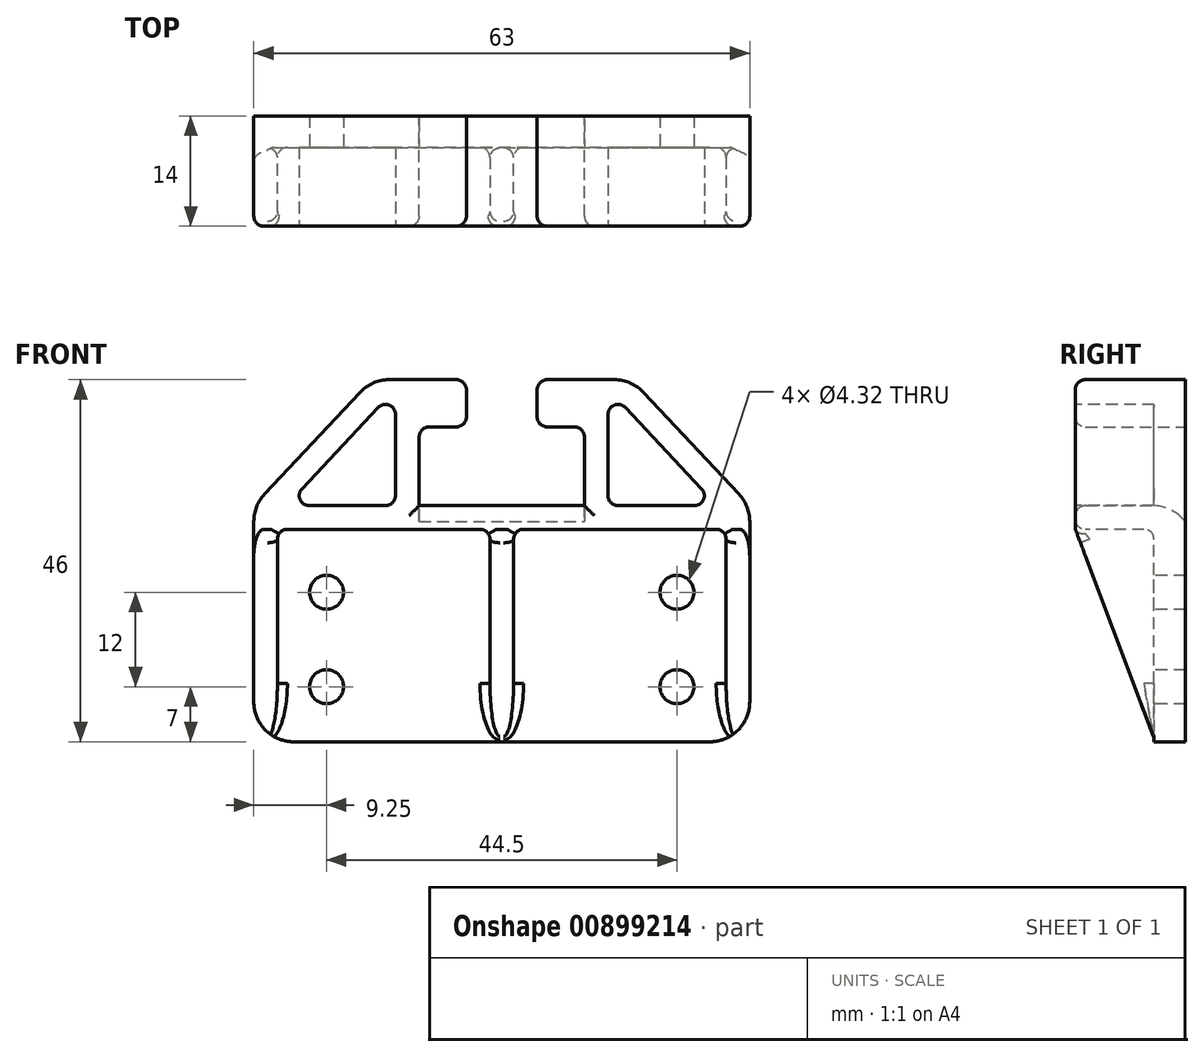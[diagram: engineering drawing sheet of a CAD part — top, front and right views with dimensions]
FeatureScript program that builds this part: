
annotation { "Feature Type Name" : "Feature", "Feature Type Description" : "" }
export const myFeature = defineFeature(function(context is Context, id is Id, definition is map)
    precondition{}
    {
        {
            var Q0;
            Q0=qCreatedBy(makeId("Front.planeOp"),FACE);
            var sketch = newSketch(context, id + "F0", { "sketchPlane" : qUnion([Q0])});
            skLineSegment(sketch, "E0", {"start": v(0, 0) * mm, "end": v(26.42, 0) * mm});
            skLineSegment(sketch, "E1", {"start": v(31.5, 5.08) * mm, "end": v(31.5, 28) * mm});
            skLineSegment(sketch, "E2", {"start": v(30.13, 31.47) * mm, "end": v(18, 44.4) * mm});
            skLineSegment(sketch, "E3", {"start": v(14.3, 46) * mm, "end": v(5.77, 46) * mm});
            skLineSegment(sketch, "E4", {"start": v(4.5, 44.73) * mm, "end": v(4.5, 41.27) * mm});
            skLineSegment(sketch, "E5", {"start": v(5.77, 40) * mm, "end": v(9.23, 40) * mm});
            skLineSegment(sketch, "E6", {"start": v(10.5, 38.73) * mm, "end": v(10.5, 30) * mm});
            skLineSegment(sketch, "E7", {"start": v(10.5, 30) * mm, "end": v(0, 30) * mm});
            skPoint(sketch, "E8.visualSharp", {"position": v(31.5, 0) * mm});
            skArc(sketch, "E8.filletArc", {"start": v(26.42, 0) * mm, "mid": v(30.01, 1.49) * mm, "end": v(31.5, 5.08) * mm});
            skPoint(sketch, "E9.visualSharp", {"position": v(31.5, 30) * mm});
            skArc(sketch, "E9.filletArc", {"start": v(31.5, 28) * mm, "mid": v(31.14, 29.86) * mm, "end": v(30.13, 31.47) * mm});
            skPoint(sketch, "E10.visualSharp", {"position": v(16.5, 46) * mm});
            skArc(sketch, "E10.filletArc", {"start": v(18, 44.4) * mm, "mid": v(16.32, 45.58) * mm, "end": v(14.3, 46) * mm});
            skPoint(sketch, "E11.visualSharp", {"position": v(4.5, 46) * mm});
            skArc(sketch, "E11.filletArc", {"start": v(5.77, 46) * mm, "mid": v(4.87, 45.63) * mm, "end": v(4.5, 44.73) * mm});
            skPoint(sketch, "E12.visualSharp", {"position": v(10.5, 40) * mm});
            skArc(sketch, "E12.filletArc", {"start": v(10.5, 38.73) * mm, "mid": v(10.13, 39.63) * mm, "end": v(9.23, 40) * mm});
            skPoint(sketch, "E13.visualSharp", {"position": v(4.5, 40) * mm});
            skArc(sketch, "E13.filletArc", {"start": v(4.5, 41.27) * mm, "mid": v(4.87, 40.37) * mm, "end": v(5.77, 40) * mm});
            skArc(sketch, "E14.MirrorCS", {"start": v(-5.77, 46) * mm, "mid": v(-4.87, 45.63) * mm, "end": v(-4.5, 44.73) * mm});
            skLineSegment(sketch, "E15.MirrorCS", {"start": v(-30.13, 31.47) * mm, "end": v(-18, 44.4) * mm});
            skArc(sketch, "E16.MirrorCS", {"start": v(-26.42, 0) * mm, "mid": v(-30.01, 1.49) * mm, "end": v(-31.5, 5.08) * mm});
            skLineSegment(sketch, "E17.MirrorCS", {"start": v(-10.5, 38.73) * mm, "end": v(-10.5, 30) * mm});
            skPoint(sketch, "E18.MirrorP", {"position": v(-16.5, 46) * mm});
            skArc(sketch, "E19.MirrorCS", {"start": v(-4.5, 41.27) * mm, "mid": v(-4.87, 40.37) * mm, "end": v(-5.77, 40) * mm});
            skArc(sketch, "E20.MirrorCS", {"start": v(-10.5, 38.73) * mm, "mid": v(-10.13, 39.63) * mm, "end": v(-9.23, 40) * mm});
            skLineSegment(sketch, "E21.MirrorCS", {"start": v(-14.3, 46) * mm, "end": v(-5.77, 46) * mm});
            skArc(sketch, "E22.MirrorCS", {"start": v(-31.5, 28) * mm, "mid": v(-31.14, 29.86) * mm, "end": v(-30.13, 31.47) * mm});
            skPoint(sketch, "E23.MirrorP", {"position": v(-4.5, 46) * mm});
            skLineSegment(sketch, "E24.MirrorCS", {"start": v(0, 0) * mm, "end": v(-26.42, 0) * mm});
            skLineSegment(sketch, "E25.MirrorCS", {"start": v(-4.5, 44.73) * mm, "end": v(-4.5, 41.27) * mm});
            skPoint(sketch, "E26.MirrorP", {"position": v(-10.5, 40) * mm});
            skArc(sketch, "E27.MirrorCS", {"start": v(-18, 44.4) * mm, "mid": v(-16.32, 45.58) * mm, "end": v(-14.3, 46) * mm});
            skLineSegment(sketch, "E28.MirrorCS", {"start": v(-31.5, 5.08) * mm, "end": v(-31.5, 28) * mm});
            skPoint(sketch, "E29.MirrorP", {"position": v(-31.5, 0) * mm});
            skPoint(sketch, "E30.MirrorP", {"position": v(-4.5, 40) * mm});
            skLineSegment(sketch, "E31.MirrorCS", {"start": v(-10.5, 30) * mm, "end": v(0, 30) * mm});
            skLineSegment(sketch, "E32.MirrorCS", {"start": v(-5.77, 40) * mm, "end": v(-9.23, 40) * mm});
            skPoint(sketch, "E33.MirrorP", {"position": v(-31.5, 30) * mm});
            skSolve(sketch);
        }
        {
            var Q0;
            Q0 = qSketchRegion(id + "F0", true);
            extrude(context, id + "F1", {"entities" : qUnion([Q0]), "depth" : 14 * mm, "offsetDistance" : 25.4 * mm});
        }
        {
            var Q0;
            Q0=makeQuery(id+"F1.opExtrude","CAP_FACE",FACE,{"disambiguationData":[OSD([sQuery(id+"F0.wireOp",EDGE,"E0"),sQuery(id+"F0.wireOp",EDGE,"E1"),sQuery(id+"F0.wireOp",EDGE,"E2"),sQuery(id+"F0.wireOp",EDGE,"E3"),sQuery(id+"F0.wireOp",EDGE,"E4"),sQuery(id+"F0.wireOp",EDGE,"E5"),sQuery(id+"F0.wireOp",EDGE,"E6"),sQuery(id+"F0.wireOp",EDGE,"E7"),sQuery(id+"F0.wireOp",EDGE,"E8.filletArc"),sQuery(id+"F0.wireOp",EDGE,"E9.filletArc"),sQuery(id+"F0.wireOp",EDGE,"E10.filletArc"),sQuery(id+"F0.wireOp",EDGE,"E11.filletArc"),sQuery(id+"F0.wireOp",EDGE,"E12.filletArc"),sQuery(id+"F0.wireOp",EDGE,"E13.filletArc"),sQuery(id+"F0.wireOp",EDGE,"E14.MirrorCS"),sQuery(id+"F0.wireOp",EDGE,"E15.MirrorCS"),sQuery(id+"F0.wireOp",EDGE,"E16.MirrorCS"),sQuery(id+"F0.wireOp",EDGE,"E17.MirrorCS"),sQuery(id+"F0.wireOp",EDGE,"E19.MirrorCS"),sQuery(id+"F0.wireOp",EDGE,"E20.MirrorCS"),sQuery(id+"F0.wireOp",EDGE,"E21.MirrorCS"),sQuery(id+"F0.wireOp",EDGE,"E22.MirrorCS"),sQuery(id+"F0.wireOp",EDGE,"E24.MirrorCS"),sQuery(id+"F0.wireOp",EDGE,"E25.MirrorCS"),sQuery(id+"F0.wireOp",EDGE,"E27.MirrorCS"),sQuery(id+"F0.wireOp",EDGE,"E28.MirrorCS"),sQuery(id+"F0.wireOp",EDGE,"E31.MirrorCS"),sQuery(id+"F0.wireOp",EDGE,"E32.MirrorCS")])],"isStart":false});
            var sketch = newSketch(context, id + "F2", { "sketchPlane" : qUnion([Q0])});
            skLineSegment(sketch, "E34.bottom", {"start": v(22.25, 7) * mm, "end": v(-22.25, 7) * mm});
            skLineSegment(sketch, "E34.top", {"start": v(22.25, 19) * mm, "end": v(-22.25, 19) * mm});
            skLineSegment(sketch, "E34.left", {"start": v(22.25, 7) * mm, "end": v(22.25, 19) * mm});
            skLineSegment(sketch, "E34.right", {"start": v(-22.25, 7) * mm, "end": v(-22.25, 19) * mm});
            skPoint(sketch, "E34.middle", {"position": v(0, 13) * mm});
            skLineSegment(sketch, "E35", {"start": v(0, 0) * mm, "end": v(0, 13) * mm});
            skSolve(sketch);
        }
        {
            var Q0;
            Q0=sQuery(id+"F2.wireOp",VERTEX,"E34.right.end");
            var Q1;
            Q1=sQuery(id+"F2.wireOp",VERTEX,"E34.top.start");
            var Q2;
            Q2=sQuery(id+"F2.wireOp",VERTEX,"E34.bottom.start");
            var Q3;
            Q3=sQuery(id+"F2.wireOp",VERTEX,"E34.right.start");
            var Q4;
            Q4=makeQuery(id+"F1.opExtrude","SWEPT_BODY",BODY,{"disambiguationData":[OSD([sQuery(id+"F0.wireOp",EDGE,"E0"),sQuery(id+"F0.wireOp",EDGE,"E1"),sQuery(id+"F0.wireOp",EDGE,"E2"),sQuery(id+"F0.wireOp",EDGE,"E3"),sQuery(id+"F0.wireOp",EDGE,"E4"),sQuery(id+"F0.wireOp",EDGE,"E5"),sQuery(id+"F0.wireOp",EDGE,"E6"),sQuery(id+"F0.wireOp",EDGE,"E7"),sQuery(id+"F0.wireOp",EDGE,"E8.filletArc"),sQuery(id+"F0.wireOp",EDGE,"E9.filletArc"),sQuery(id+"F0.wireOp",EDGE,"E10.filletArc"),sQuery(id+"F0.wireOp",EDGE,"E11.filletArc"),sQuery(id+"F0.wireOp",EDGE,"E12.filletArc"),sQuery(id+"F0.wireOp",EDGE,"E13.filletArc"),sQuery(id+"F0.wireOp",EDGE,"E14.MirrorCS"),sQuery(id+"F0.wireOp",EDGE,"E15.MirrorCS"),sQuery(id+"F0.wireOp",EDGE,"E16.MirrorCS"),sQuery(id+"F0.wireOp",EDGE,"E17.MirrorCS"),sQuery(id+"F0.wireOp",EDGE,"E19.MirrorCS"),sQuery(id+"F0.wireOp",EDGE,"E20.MirrorCS"),sQuery(id+"F0.wireOp",EDGE,"E21.MirrorCS"),sQuery(id+"F0.wireOp",EDGE,"E22.MirrorCS"),sQuery(id+"F0.wireOp",EDGE,"E24.MirrorCS"),sQuery(id+"F0.wireOp",EDGE,"E25.MirrorCS"),sQuery(id+"F0.wireOp",EDGE,"E27.MirrorCS"),sQuery(id+"F0.wireOp",EDGE,"E28.MirrorCS"),sQuery(id+"F0.wireOp",EDGE,"E31.MirrorCS"),sQuery(id+"F0.wireOp",EDGE,"E32.MirrorCS")])]});
            hole(context, id + "F3", {"style" : HoleStyle.SIMPLE, "endStyle" : HoleEndStyle.THROUGH, "standardTappedOrClearance" : lookupTablePath({ "standard" : "ANSI", "fit" : "Normal (ASME)", "size" : "#6", "type" : "Clearance" }), "standardBlindInLast" : lookupTablePath({ "fit" : "Normal", "standard" : "ANSI", "size" : "#6", "type" : "Clearance" }), "holeDiameter" : 4.32 * mm, "majorDiameter" : 6.35 * mm, "isTappedThrough" : true, "tappedDepth" : 12.7 * mm, "tapClearance" : 3, "locations" : qUnion([Q0, Q1, Q2, Q3]), "scope" : qUnion([Q4])});
        }
        {
            var Q0;
            Q0=makeQuery(id+"F1.opExtrude","CAP_FACE",FACE,{"disambiguationData":[OSD([sQuery(id+"F0.wireOp",EDGE,"E0"),sQuery(id+"F0.wireOp",EDGE,"E1"),sQuery(id+"F0.wireOp",EDGE,"E2"),sQuery(id+"F0.wireOp",EDGE,"E3"),sQuery(id+"F0.wireOp",EDGE,"E4"),sQuery(id+"F0.wireOp",EDGE,"E5"),sQuery(id+"F0.wireOp",EDGE,"E6"),sQuery(id+"F0.wireOp",EDGE,"E7"),sQuery(id+"F0.wireOp",EDGE,"E8.filletArc"),sQuery(id+"F0.wireOp",EDGE,"E9.filletArc"),sQuery(id+"F0.wireOp",EDGE,"E10.filletArc"),sQuery(id+"F0.wireOp",EDGE,"E11.filletArc"),sQuery(id+"F0.wireOp",EDGE,"E12.filletArc"),sQuery(id+"F0.wireOp",EDGE,"E13.filletArc"),sQuery(id+"F0.wireOp",EDGE,"E14.MirrorCS"),sQuery(id+"F0.wireOp",EDGE,"E15.MirrorCS"),sQuery(id+"F0.wireOp",EDGE,"E16.MirrorCS"),sQuery(id+"F0.wireOp",EDGE,"E17.MirrorCS"),sQuery(id+"F0.wireOp",EDGE,"E19.MirrorCS"),sQuery(id+"F0.wireOp",EDGE,"E20.MirrorCS"),sQuery(id+"F0.wireOp",EDGE,"E21.MirrorCS"),sQuery(id+"F0.wireOp",EDGE,"E22.MirrorCS"),sQuery(id+"F0.wireOp",EDGE,"E24.MirrorCS"),sQuery(id+"F0.wireOp",EDGE,"E25.MirrorCS"),sQuery(id+"F0.wireOp",EDGE,"E27.MirrorCS"),sQuery(id+"F0.wireOp",EDGE,"E28.MirrorCS"),sQuery(id+"F0.wireOp",EDGE,"E31.MirrorCS"),sQuery(id+"F0.wireOp",EDGE,"E32.MirrorCS")])],"isStart":false});
            var sketch = newSketch(context, id + "F4", { "sketchPlane" : qUnion([Q0])});
            skLineSegment(sketch, "E36", {"start": v(-31.5, -15.35) * mm, "end": v(-31.5, 30) * mm});
            skLineSegment(sketch, "E37.0", {"start": v(-28.5, -15.35) * mm, "end": v(-28.5, 25.73) * mm});
            skLineSegment(sketch, "E38", {"start": v(-31.5, 30) * mm, "end": v(-15.25, 47.33) * mm});
            skLineSegment(sketch, "E39.0", {"start": v(-25.38, 32.14) * mm, "end": v(-15.7, 42.47) * mm});
            skLineSegment(sketch, "E40", {"start": v(-10.5, 30) * mm, "end": v(-10.5, 38.73) * mm});
            skLineSegment(sketch, "E41.0", {"start": v(-13.5, 31.27) * mm, "end": v(-13.5, 41.6) * mm});
            skLineSegment(sketch, "E42", {"start": v(-10.5, 30) * mm, "end": v(0, 30) * mm});
            skLineSegment(sketch, "E43.0", {"start": v(-13.5, 27) * mm, "end": v(-2.77, 27) * mm});
            skLineSegment(sketch, "E44", {"start": v(0, 9.73) * mm, "end": v(0, 22.22) * mm});
            skLineSegment(sketch, "E45.0", {"start": v(-1.5, 0) * mm, "end": v(-1.5, 25.73) * mm});
            skLineSegment(sketch, "E46", {"start": v(-13.5, 27) * mm, "end": v(-27.23, 27) * mm});
            skLineSegment(sketch, "E47.0", {"start": v(-14.77, 30) * mm, "end": v(-24.46, 30) * mm});
            skLineSegment(sketch, "E48", {"start": v(-1.5, 0) * mm, "end": v(-28.5, 0) * mm});
            skPoint(sketch, "E49.visualSharp", {"position": v(-27.39, 30) * mm});
            skArc(sketch, "E49.filletArc", {"start": v(-25.38, 32.14) * mm, "mid": v(-25.62, 30.77) * mm, "end": v(-24.46, 30) * mm});
            skPoint(sketch, "E50.visualSharp", {"position": v(-13.5, 44.81) * mm});
            skArc(sketch, "E50.filletArc", {"start": v(-13.5, 41.6) * mm, "mid": v(-14.3, 42.78) * mm, "end": v(-15.7, 42.47) * mm});
            skPoint(sketch, "E51.visualSharp", {"position": v(-13.5, 30) * mm});
            skArc(sketch, "E51.filletArc", {"start": v(-14.77, 30) * mm, "mid": v(-13.87, 30.37) * mm, "end": v(-13.5, 31.27) * mm});
            skPoint(sketch, "E52.visualSharp", {"position": v(-28.5, 27) * mm});
            skArc(sketch, "E52.filletArc", {"start": v(-27.23, 27) * mm, "mid": v(-28.13, 26.63) * mm, "end": v(-28.5, 25.73) * mm});
            skPoint(sketch, "E53.visualSharp", {"position": v(-1.5, 27) * mm});
            skArc(sketch, "E53.filletArc", {"start": v(-1.5, 25.73) * mm, "mid": v(-1.87, 26.63) * mm, "end": v(-2.77, 27) * mm});
            skPoint(sketch, "E54.MirrorP", {"position": v(1.5, 27) * mm});
            skPoint(sketch, "E55.MirrorP", {"position": v(28.5, 27) * mm});
            skPoint(sketch, "E56.MirrorP", {"position": v(13.5, 30) * mm});
            skLineSegment(sketch, "E57.MirrorCS", {"start": v(13.5, 27) * mm, "end": v(27.23, 27) * mm});
            skArc(sketch, "E58.MirrorCS", {"start": v(25.38, 32.14) * mm, "mid": v(25.62, 30.77) * mm, "end": v(24.46, 30) * mm});
            skArc(sketch, "E59.MirrorCS", {"start": v(1.5, 25.73) * mm, "mid": v(1.87, 26.63) * mm, "end": v(2.77, 27) * mm});
            skLineSegment(sketch, "E60.MirrorCS", {"start": v(14.77, 30) * mm, "end": v(24.46, 30) * mm});
            skLineSegment(sketch, "E61.MirrorCS", {"start": v(31.5, 30) * mm, "end": v(15.25, 47.33) * mm});
            skArc(sketch, "E62.MirrorCS", {"start": v(13.5, 41.6) * mm, "mid": v(14.3, 42.78) * mm, "end": v(15.7, 42.47) * mm});
            skLineSegment(sketch, "E63.MirrorCS", {"start": v(1.5, 0) * mm, "end": v(28.5, 0) * mm});
            skArc(sketch, "E64.MirrorCS", {"start": v(14.77, 30) * mm, "mid": v(13.87, 30.37) * mm, "end": v(13.5, 31.27) * mm});
            skLineSegment(sketch, "E65.MirrorCS", {"start": v(25.38, 32.14) * mm, "end": v(15.7, 42.47) * mm});
            skLineSegment(sketch, "E66.MirrorCS", {"start": v(13.5, 27) * mm, "end": v(2.77, 27) * mm});
            skArc(sketch, "E67.MirrorCS", {"start": v(27.23, 27) * mm, "mid": v(28.13, 26.63) * mm, "end": v(28.5, 25.73) * mm});
            skLineSegment(sketch, "E68.MirrorCS", {"start": v(10.5, 30) * mm, "end": v(10.5, 38.73) * mm});
            skPoint(sketch, "E69.MirrorP", {"position": v(13.5, 44.81) * mm});
            skPoint(sketch, "E70.MirrorP", {"position": v(27.39, 30) * mm});
            skLineSegment(sketch, "E71.MirrorCS", {"start": v(13.5, 31.27) * mm, "end": v(13.5, 41.6) * mm});
            skLineSegment(sketch, "E72.MirrorCS", {"start": v(1.5, 0) * mm, "end": v(1.5, 25.73) * mm});
            skLineSegment(sketch, "E73.MirrorCS", {"start": v(28.5, -15.35) * mm, "end": v(28.5, 25.73) * mm});
            skSolve(sketch);
        }
        {
            var Q0;
            Q0 = qSketchRegion(id + "F4", true);
            extrude(context, id + "F5", {"entities" : qUnion([Q0]), "operationType" : NewBodyOperationType.REMOVE, "oppositeDirection" : true, "depth" : 10 * mm, "offsetDistance" : 25.4 * mm});
        }
        {
            var Q0;
            Q0=makeQuery(id+"F5.boolean.opBoolean","COPY",FACE,{"derivedFrom":makeQuery(id+"F5.opExtrude","SWEPT_FACE",FACE,{"disambiguationData":[OSD([sQuery(id+"F4.wireOp",EDGE,"E73.MirrorCS")])]})});
            var sketch = newSketch(context, id + "F6", { "sketchPlane" : qUnion([Q0])});
            skLineSegment(sketch, "E74", {"start": v(4, 0.45) * mm, "end": v(14, 27) * mm});
            skLineSegment(sketch, "E75", {"start": v(14, 27) * mm, "end": v(14, 0.45) * mm});
            skLineSegment(sketch, "E76", {"start": v(14, 0.45) * mm, "end": v(14, -0.72) * mm});
            skLineSegment(sketch, "E77", {"start": v(14, -0.72) * mm, "end": v(4, -0.72) * mm});
            skLineSegment(sketch, "E78", {"start": v(4, -0.72) * mm, "end": v(4, 0.45) * mm});
            skSolve(sketch);
        }
        {
            var Q0;
            Q0 = qSketchRegion(id + "F6", true);
            extrude(context, id + "F7", {"entities" : qUnion([Q0]), "operationType" : NewBodyOperationType.REMOVE, "oppositeDirection" : true, "depth" : 127 * mm, "offsetDistance" : 25.4 * mm, "symmetric" : true});
        }
        {
            var Q0;
            Q0=makeQuery(id+"F5.boolean.opBoolean","COPY",EDGE,{"derivedFrom":makeQuery(id+"F5.opExtrude","CAP_EDGE",EDGE,{"disambiguationData":[OSD([sQuery(id+"F4.wireOp",EDGE,"E65.MirrorCS")])],"isStart":true})});
            var Q1;
            Q1=makeQuery(id+"F5.boolean.opBoolean","COPY",EDGE,{"derivedFrom":makeQuery(id+"F5.opExtrude","CAP_EDGE",EDGE,{"disambiguationData":[OSD([sQuery(id+"F4.wireOp",EDGE,"E41.0")])],"isStart":true})});
            var Q2;
            Q2=makeQuery(id+"F5.boolean.opBoolean","COPY",EDGE,{"derivedFrom":makeQuery(id+"F5.opExtrude","CAP_EDGE",EDGE,{"disambiguationData":[OSD([sQuery(id+"F4.wireOp",EDGE,"E57.MirrorCS"),sQuery(id+"F4.wireOp",EDGE,"E66.MirrorCS")])],"isStart":true})});
            var Q3;
            Q3=makeQuery(id+"F5.boolean.opBoolean","COPY",EDGE,{"derivedFrom":makeQuery(id+"F5.opExtrude","CAP_EDGE",EDGE,{"disambiguationData":[OSD([sQuery(id+"F4.wireOp",EDGE,"E43.0"),sQuery(id+"F4.wireOp",EDGE,"E46")])],"isStart":true})});
            var Q4;
            Q4=makeQuery(id+"F7.boolean.opBoolean","INTERSECT",EDGE,{"derivedFrom":[makeQuery(id+"F5.boolean.opBoolean","COPY",FACE,{"derivedFrom":makeQuery(id+"F5.opExtrude","SWEPT_FACE",FACE,{"disambiguationData":[OSD([sQuery(id+"F4.wireOp",EDGE,"E45.0")])]})}),makeQuery(id+"F7.opExtrude","SWEPT_FACE",FACE,{"disambiguationData":[OSD([sQuery(id+"F6.wireOp",EDGE,"E74")])]})]});
            var Q5;
            Q5=makeQuery(id+"F7.boolean.opBoolean","INTERSECT",EDGE,{"derivedFrom":[makeQuery(id+"F5.boolean.opBoolean","COPY",FACE,{"derivedFrom":makeQuery(id+"F5.opExtrude","SWEPT_FACE",FACE,{"disambiguationData":[OSD([sQuery(id+"F4.wireOp",EDGE,"E72.MirrorCS")])]})}),makeQuery(id+"F7.opExtrude","SWEPT_FACE",FACE,{"disambiguationData":[OSD([sQuery(id+"F6.wireOp",EDGE,"E74")])]})]});
            var Q6;
            Q6=makeQuery(id+"F7.boolean.opBoolean","INTERSECT",EDGE,{"derivedFrom":[makeQuery(id+"F5.boolean.opBoolean","COPY",FACE,{"derivedFrom":makeQuery(id+"F5.opExtrude","SWEPT_FACE",FACE,{"disambiguationData":[OSD([sQuery(id+"F4.wireOp",EDGE,"E73.MirrorCS")])]})}),makeQuery(id+"F7.opExtrude","SWEPT_FACE",FACE,{"disambiguationData":[OSD([sQuery(id+"F6.wireOp",EDGE,"E74")])]})]});
            var Q7;
            Q7=makeQuery(id+"F7.boolean.opBoolean","INTERSECT",EDGE,{"derivedFrom":[makeQuery(id+"F5.boolean.opBoolean","COPY",FACE,{"derivedFrom":makeQuery(id+"F5.opExtrude","SWEPT_FACE",FACE,{"disambiguationData":[OSD([sQuery(id+"F4.wireOp",EDGE,"E37.0")])]})}),makeQuery(id+"F7.opExtrude","SWEPT_FACE",FACE,{"disambiguationData":[OSD([sQuery(id+"F6.wireOp",EDGE,"E74")])]})]});
            fillet(context, id + "F8", {"entities" : qUnion([Q0, Q1, Q2, Q3, Q4, Q5, Q6, Q7]), "radius" : 1.27 * mm, "tangentPropagation" : true, "allowEdgeOverflow" : false});
        }
        {
            var Q0;
            Q0=makeQuery(id+"F5.boolean.opBoolean","COPY",EDGE,{"derivedFrom":makeQuery(id+"F5.opExtrude","CAP_EDGE",EDGE,{"disambiguationData":[OSD([sQuery(id+"F4.wireOp",EDGE,"E57.MirrorCS"),sQuery(id+"F4.wireOp",EDGE,"E66.MirrorCS")])],"isStart":false})});
            fillet(context, id + "F9", {"entities" : qUnion([Q0]), "radius" : 1.27 * mm, "tangentPropagation" : true, "allowEdgeOverflow" : false});
        }
        {
            var Q0;
            Q0=makeQuery(id+"F7.boolean.opBoolean","MERGE",EDGE,{"derivedFrom":[makeQuery(id+"F5.boolean.opBoolean","COPY",EDGE,{"derivedFrom":makeQuery(id+"F5.opExtrude","CAP_EDGE",EDGE,{"disambiguationData":[OSD([sQuery(id+"F4.wireOp",EDGE,"E48")])],"isStart":false})}),makeQuery(id+"F5.boolean.opBoolean","COPY",EDGE,{"derivedFrom":makeQuery(id+"F5.opExtrude","CAP_EDGE",EDGE,{"disambiguationData":[OSD([sQuery(id+"F4.wireOp",EDGE,"E63.MirrorCS")])],"isStart":false})})]});
            var Q1;
            Q1=makeQuery(id+"F1.opExtrude","CAP_EDGE",EDGE,{"disambiguationData":[OSD([sQuery(id+"F0.wireOp",EDGE,"E15.MirrorCS")])],"isStart":false});
            var Q2;
            Q2=makeQuery(id+"F1.opExtrude","CAP_EDGE",EDGE,{"disambiguationData":[OSD([sQuery(id+"F0.wireOp",EDGE,"E2")])],"isStart":false});
            var Q3;
            Q3=makeQuery(id+"F1.opExtrude","CAP_EDGE",EDGE,{"disambiguationData":[OSD([sQuery(id+"F0.wireOp",EDGE,"E7"),sQuery(id+"F0.wireOp",EDGE,"E31.MirrorCS")])],"isStart":false});
            fillet(context, id + "F10", {"entities" : qUnion([Q0, Q1, Q2, Q3]), "radius" : 1.27 * mm, "tangentPropagation" : true, "allowEdgeOverflow" : false});
        }
        {
            var Q0;
            Q0=makeQuery(id+"F1.opExtrude","CAP_EDGE",EDGE,{"disambiguationData":[OSD([sQuery(id+"F0.wireOp",EDGE,"E7"),sQuery(id+"F0.wireOp",EDGE,"E31.MirrorCS")])],"isStart":true});
            chamfer(context, id + "F11", {"entities" : qUnion([Q0]), "width" : 2.03 * mm, "tangentPropagation" : true});
        }
        {
            var Q0;
            {var subQ0=sQuery(id+"F0.wireOp",EDGE,"E31.MirrorCS");var subQ1=sQuery(id+"F0.wireOp",EDGE,"E7");Q0=makeQuery(id+"F11.opChamfer","BLEND_EDGE",EDGE,{"blendedFrom":[makeQuery(id+"F1.opExtrude","CAP_EDGE",EDGE,{"disambiguationData":[OSD([subQ1,subQ0])],"isStart":true}),makeQuery(id+"F1.opExtrude","SWEPT_FACE",FACE,{"disambiguationData":[OSD([subQ1,subQ0])]})],"blendedInto":[makeQuery(id+"F1.opExtrude","SWEPT_FACE",FACE,{"disambiguationData":[OSD([subQ1,subQ0])]})]});}
            fillet(context, id + "F12", {"entities" : qUnion([Q0]), "radius" : 5.08 * mm, "tangentPropagation" : true, "allowEdgeOverflow" : false});
        }
    });
